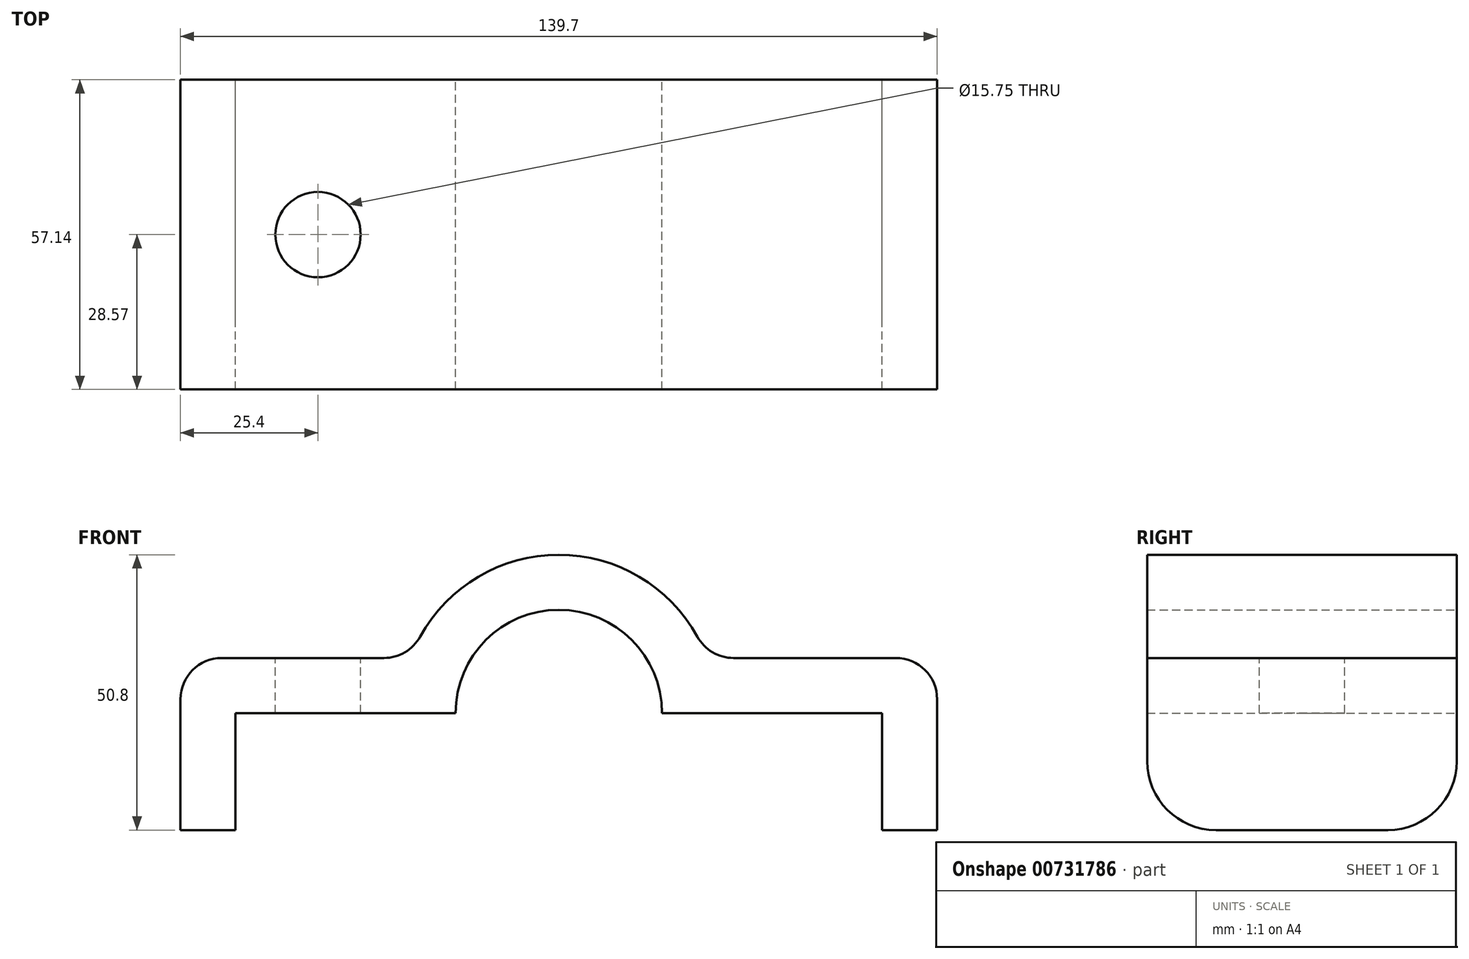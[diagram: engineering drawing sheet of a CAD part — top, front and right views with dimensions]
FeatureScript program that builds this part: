
annotation { "Feature Type Name" : "Feature", "Feature Type Description" : "" }
export const myFeature = defineFeature(function(context is Context, id is Id, definition is map)
    precondition{}
    {
        {
            var Q0;
            Q0=qCreatedBy(makeId("Front.planeOp"),FACE);
            var sketch = newSketch(context, id + "F0", { "sketchPlane" : qUnion([Q0])});
            skArc(sketch, "E0", {"start": v(19.05, 0) * mm, "mid": v(0, 19.05) * mm, "end": v(-19.05, 0) * mm});
            skLineSegment(sketch, "E1", {"start": v(-19.05, 0) * mm, "end": v(-59.7, 0) * mm});
            skLineSegment(sketch, "E2", {"start": v(-59.7, 0) * mm, "end": v(-59.7, -21.6) * mm});
            skLineSegment(sketch, "E3", {"start": v(-59.7, -21.6) * mm, "end": v(-69.85, -21.6) * mm});
            skLineSegment(sketch, "E4", {"start": v(-69.85, -21.6) * mm, "end": v(-69.85, 2.54) * mm});
            skLineSegment(sketch, "E5", {"start": v(-62.23, 10.16) * mm, "end": v(-32.25, 10.16) * mm});
            skPoint(sketch, "E6", {"position": v(-39.37, 0) * mm});
            skArc(sketch, "E7", {"start": v(25.58, 14.1) * mm, "mid": v(0, 29.21) * mm, "end": v(-25.58, 14.1) * mm});
            skPoint(sketch, "E8.visualSharp", {"position": v(-69.85, 10.16) * mm});
            skArc(sketch, "E8.filletArc", {"start": v(-62.23, 10.16) * mm, "mid": v(-67.62, 7.93) * mm, "end": v(-69.85, 2.54) * mm});
            skPoint(sketch, "E9.visualSharp", {"position": v(-27.39, 10.16) * mm});
            skArc(sketch, "E9.filletArc", {"start": v(-32.25, 10.16) * mm, "mid": v(-28.38, 11.22) * mm, "end": v(-25.58, 14.1) * mm});
            skLineSegment(sketch, "E10.MirrorCS", {"start": v(62.23, 10.16) * mm, "end": v(32.25, 10.16) * mm});
            skArc(sketch, "E11.MirrorCS", {"start": v(62.23, 10.16) * mm, "mid": v(67.62, 7.93) * mm, "end": v(69.85, 2.54) * mm});
            skLineSegment(sketch, "E12.MirrorCS", {"start": v(69.85, -21.6) * mm, "end": v(69.85, 2.54) * mm});
            skLineSegment(sketch, "E13.MirrorCS", {"start": v(59.7, -21.6) * mm, "end": v(69.85, -21.6) * mm});
            skLineSegment(sketch, "E14.MirrorCS", {"start": v(59.7, 0) * mm, "end": v(59.7, -21.6) * mm});
            skLineSegment(sketch, "E15.MirrorCS", {"start": v(19.05, 0) * mm, "end": v(59.7, 0) * mm});
            skPoint(sketch, "E16.newPointA", {"position": v(32.25, 10.16) * mm});
            skArc(sketch, "E16.filletArc", {"start": v(25.58, 14.1) * mm, "mid": v(28.38, 11.22) * mm, "end": v(32.25, 10.16) * mm});
            skSolve(sketch);
        }
        {
            var Q0;
            Q0=makeQuery(id+"F0.imprint","IMPRINT",FACE,{"disambiguationData":[TD([[makeQuery(id+"F0.imprint","IMPRINT",EDGE,{"derivedFrom":sQuery(id+"F0.wireOp",EDGE,"E0")}),-1.0]])]});
            extrude(context, id + "F1", {"entities" : qUnion([Q0]), "endBound" : BoundingType.SYMMETRIC, "depth" : 57.15 * mm, "offsetDistance" : 25.4 * mm});
        }
        {
            var Q0;
            Q0=makeQuery(id+"F1.opExtrude","CAP_EDGE",EDGE,{"disambiguationData":[OSD([sQuery(id+"F0.wireOp",EDGE,"E13.MirrorCS")])],"isStart":false});
            var Q1;
            Q1=makeQuery(id+"F1.opExtrude","CAP_EDGE",EDGE,{"disambiguationData":[OSD([sQuery(id+"F0.wireOp",EDGE,"E3")])],"isStart":false});
            var Q2;
            Q2=makeQuery(id+"F1.opExtrude","CAP_EDGE",EDGE,{"disambiguationData":[OSD([sQuery(id+"F0.wireOp",EDGE,"E13.MirrorCS")])],"isStart":true});
            var Q3;
            Q3=makeQuery(id+"F1.opExtrude","CAP_EDGE",EDGE,{"disambiguationData":[OSD([sQuery(id+"F0.wireOp",EDGE,"E3")])],"isStart":true});
            fillet(context, id + "F2", {"entities" : qUnion([Q0, Q1, Q2, Q3]), "radius" : 12.7 * mm, "tangentPropagation" : true, "allowEdgeOverflow" : false});
        }
        {
            var Q0;
            Q0=makeQuery(id+"F1.opExtrude","SWEPT_FACE",FACE,{"disambiguationData":[OSD([sQuery(id+"F0.wireOp",EDGE,"E5")])]});
            var sketch = newSketch(context, id + "F3", { "sketchPlane" : qUnion([Q0])});
            skCircle(sketch, "E17", {"center": v(-44.45, 0) * mm, "radius": 7.87 * mm});
            skCircle(sketch, "E18.MirrorC", {"center": v(44.45, 0) * mm, "radius": 7.87 * mm});
            skSolve(sketch);
        }
        {
            var Q0;
            Q0=makeQuery(id+"F3.imprint","IMPRINT",FACE,{"disambiguationData":[TD([[makeQuery(id+"F3.imprint","IMPRINT",EDGE,{"derivedFrom":sQuery(id+"F3.wireOp",EDGE,"E17")}),1.0]])]});
            var Q1;
            Q1=makeQuery(id+"F3.imprint","IMPRINT",FACE,{"disambiguationData":[TD([[makeQuery(id+"F3.imprint","IMPRINT",EDGE,{"derivedFrom":sQuery(id+"F3.wireOp",EDGE,"E18.MirrorC")}),-1.0]])]});
            extrude(context, id + "F4", {"entities" : qUnion([Q0, Q1]), "operationType" : NewBodyOperationType.REMOVE, "oppositeDirection" : true, "depth" : 10.16 * mm, "offsetDistance" : 25.4 * mm});
        }
    });
